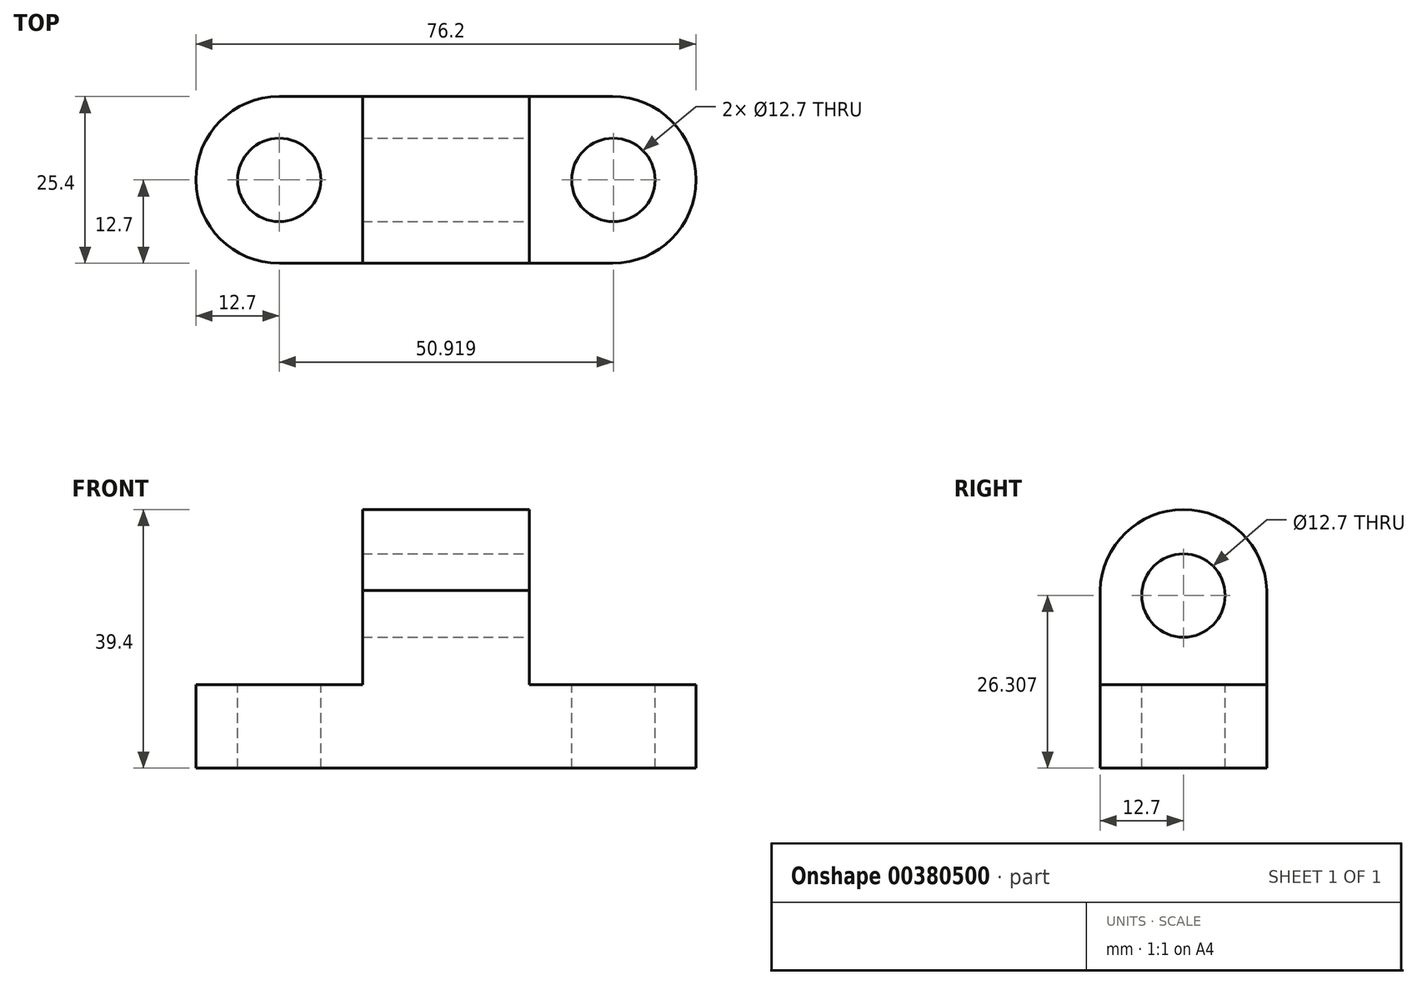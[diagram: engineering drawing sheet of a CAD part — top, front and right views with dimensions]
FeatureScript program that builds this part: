
annotation { "Feature Type Name" : "Feature", "Feature Type Description" : "" }
export const myFeature = defineFeature(function(context is Context, id is Id, definition is map)
    precondition{}
    {
        {
            var Q0;
            Q0=qCreatedBy(makeId("Front.planeOp"),FACE);
            var sketch = newSketch(context, id + "F0", { "sketchPlane" : qUnion([Q0])});
            skLineSegment(sketch, "E0", {"start": v(0, 0) * mm, "end": v(76.2, 0) * mm});
            skLineSegment(sketch, "E1", {"start": v(76.2, 0) * mm, "end": v(76.2, 12.7) * mm});
            skLineSegment(sketch, "E2", {"start": v(76.2, 12.7) * mm, "end": v(50.8, 12.7) * mm});
            skLineSegment(sketch, "E3", {"start": v(50.8, 12.7) * mm, "end": v(50.8, 39.91) * mm});
            skLineSegment(sketch, "E4", {"start": v(50.8, 39.91) * mm, "end": v(25.4, 39.91) * mm});
            skLineSegment(sketch, "E5", {"start": v(25.4, 39.91) * mm, "end": v(25.4, 12.7) * mm});
            skLineSegment(sketch, "E6", {"start": v(25.4, 12.7) * mm, "end": v(0, 12.7) * mm});
            skLineSegment(sketch, "E7", {"start": v(0, 12.7) * mm, "end": v(0, 0) * mm});
            skSolve(sketch);
        }
        {
            var Q0;
            Q0=makeQuery(id+"F0.imprint","IMPRINT",FACE,{"disambiguationData":[TD([[makeQuery(id+"F0.imprint","IMPRINT",EDGE,{"derivedFrom":sQuery(id+"F0.wireOp",EDGE,"E0")}),1.0]])]});
            extrude(context, id + "F1", {"entities" : qUnion([Q0]), "depth" : 25.4 * mm});
        }
        {
            var Q0;
            Q0=makeQuery(id+"F1.opExtrude","SWEPT_FACE",FACE,{"disambiguationData":[OSD([sQuery(id+"F0.wireOp",EDGE,"E2")])]});
            var sketch = newSketch(context, id + "F2", { "sketchPlane" : qUnion([Q0])});
            skCircle(sketch, "E8", {"center": v(63.62, -12.7) * mm, "radius": 6.35 * mm});
            skSolve(sketch);
        }
        {
            var Q0;
            Q0=makeQuery(id+"F2.imprint","IMPRINT",FACE,{"disambiguationData":[TD([[makeQuery(id+"F2.imprint","IMPRINT",EDGE,{"derivedFrom":sQuery(id+"F2.wireOp",EDGE,"E8")}),1.0]])]});
            extrude(context, id + "F3", {"entities" : qUnion([Q0]), "operationType" : NewBodyOperationType.REMOVE, "oppositeDirection" : true, "depth" : 12.7 * mm});
        }
        {
            var Q0;
            Q0=makeQuery(id+"F1.opExtrude","SWEPT_FACE",FACE,{"disambiguationData":[OSD([sQuery(id+"F0.wireOp",EDGE,"E2")])]});
            var sketch = newSketch(context, id + "F4", { "sketchPlane" : qUnion([Q0])});
            skArc(sketch, "E9", {"start": v(63.5, -25.4) * mm, "mid": v(76.2, -12.7) * mm, "end": v(63.5, 0) * mm});
            skSolve(sketch);
        }
        {
            var Q0;
            {var subQ0=sQuery(id+"F4.wireOp",EDGE,"E9");var subQ1=sQuery(id+"F0.wireOp",EDGE,"E2");var subQ2=makeQuery(id+"F1.opExtrude","CAP_EDGE",EDGE,{"disambiguationData":[OSD([subQ1])],"isStart":true});var subQ3=makeQuery(id+"F4.imprint","INTERSECT",VERTEX,{"derivedFrom":[subQ2,subQ0]});Q0=makeQuery(id+"F4.imprint","IMPRINT",FACE,{"disambiguationData":[TD([[makeQuery(id+"F4.imprint","IMPRINT",EDGE,{"disambiguationData":[TD([[subQ3,1.0]])],"derivedFrom":subQ0}),-1.0]])]});}
            var Q1;
            {var subQ0=sQuery(id+"F4.wireOp",EDGE,"E9");var subQ1=sQuery(id+"F0.wireOp",EDGE,"E2");var subQ2=makeQuery(id+"F1.opExtrude","CAP_EDGE",EDGE,{"disambiguationData":[OSD([subQ1])],"isStart":false});var subQ3=makeQuery(id+"F4.imprint","INTERSECT",VERTEX,{"derivedFrom":[subQ2,subQ0]});Q1=makeQuery(id+"F4.imprint","IMPRINT",FACE,{"disambiguationData":[TD([[makeQuery(id+"F4.imprint","IMPRINT",EDGE,{"disambiguationData":[TD([[subQ3,-1.0]])],"derivedFrom":subQ0}),-1.0]])]});}
            extrude(context, id + "F5", {"entities" : qUnion([Q0, Q1]), "operationType" : NewBodyOperationType.REMOVE, "oppositeDirection" : true, "depth" : 12.7 * mm});
        }
        {
            var Q0;
            Q0=makeQuery(id+"F1.opExtrude","SWEPT_FACE",FACE,{"disambiguationData":[OSD([sQuery(id+"F0.wireOp",EDGE,"E6")])]});
            var sketch = newSketch(context, id + "F6", { "sketchPlane" : qUnion([Q0])});
            skCircle(sketch, "E10", {"center": v(12.7, -12.7) * mm, "radius": 6.35 * mm});
            skSolve(sketch);
        }
        {
            var Q0;
            Q0=makeQuery(id+"F6.imprint","IMPRINT",FACE,{"disambiguationData":[TD([[makeQuery(id+"F6.imprint","IMPRINT",EDGE,{"derivedFrom":sQuery(id+"F6.wireOp",EDGE,"E10")}),1.0]])]});
            extrude(context, id + "F7", {"entities" : qUnion([Q0]), "operationType" : NewBodyOperationType.REMOVE, "oppositeDirection" : true, "depth" : 12.7 * mm});
        }
        {
            var Q0;
            Q0=makeQuery(id+"F1.opExtrude","SWEPT_FACE",FACE,{"disambiguationData":[OSD([sQuery(id+"F0.wireOp",EDGE,"E6")])]});
            var sketch = newSketch(context, id + "F8", { "sketchPlane" : qUnion([Q0])});
            skArc(sketch, "E11", {"start": v(12.7, 0) * mm, "mid": v(0, -12.7) * mm, "end": v(12.7, -25.4) * mm});
            skSolve(sketch);
        }
        {
            var Q0;
            {var subQ0=sQuery(id+"F8.wireOp",EDGE,"E11");var subQ1=sQuery(id+"F0.wireOp",EDGE,"E6");var subQ2=makeQuery(id+"F1.opExtrude","CAP_EDGE",EDGE,{"disambiguationData":[OSD([subQ1])],"isStart":false});var subQ3=makeQuery(id+"F8.imprint","INTERSECT",VERTEX,{"derivedFrom":[subQ2,subQ0]});Q0=makeQuery(id+"F8.imprint","IMPRINT",FACE,{"disambiguationData":[TD([[makeQuery(id+"F8.imprint","IMPRINT",EDGE,{"disambiguationData":[TD([[subQ3,1.0]])],"derivedFrom":subQ0}),-1.0]])]});}
            var Q1;
            {var subQ0=sQuery(id+"F8.wireOp",EDGE,"E11");var subQ1=sQuery(id+"F0.wireOp",EDGE,"E6");var subQ2=makeQuery(id+"F1.opExtrude","CAP_EDGE",EDGE,{"disambiguationData":[OSD([subQ1])],"isStart":true});var subQ3=makeQuery(id+"F8.imprint","INTERSECT",VERTEX,{"derivedFrom":[subQ2,subQ0]});Q1=makeQuery(id+"F8.imprint","IMPRINT",FACE,{"disambiguationData":[TD([[makeQuery(id+"F8.imprint","IMPRINT",EDGE,{"disambiguationData":[TD([[subQ3,-1.0]])],"derivedFrom":subQ0}),-1.0]])]});}
            extrude(context, id + "F9", {"entities" : qUnion([Q0, Q1]), "operationType" : NewBodyOperationType.REMOVE, "oppositeDirection" : true, "depth" : 12.7 * mm});
        }
        {
            var Q0;
            Q0=makeQuery(id+"F1.opExtrude","SWEPT_FACE",FACE,{"disambiguationData":[OSD([sQuery(id+"F0.wireOp",EDGE,"E3")])]});
            var sketch = newSketch(context, id + "F10", { "sketchPlane" : qUnion([Q0])});
            skCircle(sketch, "E12", {"center": v(-12.7, 26.3) * mm, "radius": 6.35 * mm});
            skPoint(sketch, "E12.centerSnap0", {"position": v(-25.4, 26.3) * mm});
            skSolve(sketch);
        }
        {
            var Q0;
            Q0=makeQuery(id+"F10.imprint","IMPRINT",FACE,{"disambiguationData":[TD([[makeQuery(id+"F10.imprint","IMPRINT",EDGE,{"derivedFrom":sQuery(id+"F10.wireOp",EDGE,"E12")}),1.0]])]});
            extrude(context, id + "F11", {"entities" : qUnion([Q0]), "operationType" : NewBodyOperationType.REMOVE, "oppositeDirection" : true, "depth" : 25.4 * mm});
        }
        {
            var Q0;
            Q0=makeQuery(id+"F1.opExtrude","SWEPT_FACE",FACE,{"disambiguationData":[OSD([sQuery(id+"F0.wireOp",EDGE,"E3")])]});
            var sketch = newSketch(context, id + "F12", { "sketchPlane" : qUnion([Q0])});
            skArc(sketch, "E13", {"start": v(0, 26.3) * mm, "mid": v(-12.7, 39.4) * mm, "end": v(-25.4, 26.3) * mm});
            skSolve(sketch);
        }
        {
            var Q0;
            {var subQ1=sQuery(id+"F0.wireOp",EDGE,"E3");var subQ6=makeQuery(id+"F1.opExtrude","SWEPT_EDGE",EDGE,{"disambiguationData":[OSD([subQ1,sQuery(id+"F0.wireOp",EDGE,"E4")])]});Q0=makeQuery(id+"F12.imprint","IMPRINT",FACE,{"disambiguationData":[TD([[makeQuery(id+"F12.imprint","IMPRINT",EDGE,{"derivedFrom":subQ6}),-1.0]])]});}
            extrude(context, id + "F13", {"entities" : qUnion([Q0]), "operationType" : NewBodyOperationType.REMOVE, "oppositeDirection" : true, "depth" : 25.4 * mm});
        }
    });
